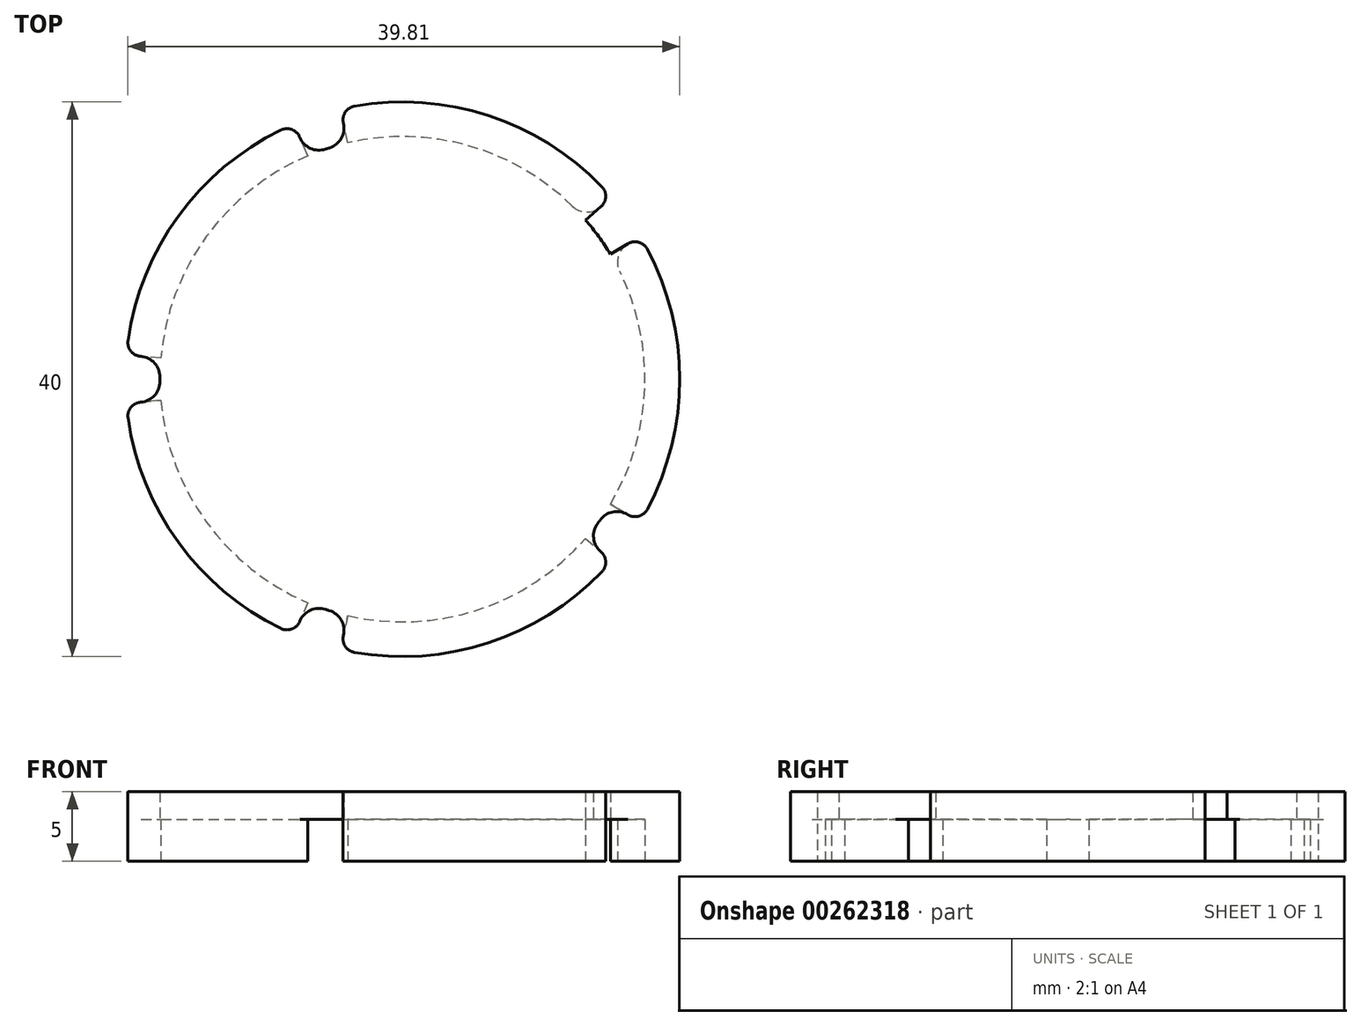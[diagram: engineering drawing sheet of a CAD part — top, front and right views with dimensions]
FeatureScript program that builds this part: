
annotation { "Feature Type Name" : "Feature", "Feature Type Description" : "" }
export const myFeature = defineFeature(function(context is Context, id is Id, definition is map)
    precondition{}
    {
        {
            var Q0;
            Q0=qCreatedBy(makeId("Top.planeOp"),FACE);
            var sketch = newSketch(context, id + "F0", { "sketchPlane" : qUnion([Q0])});
            skCircle(sketch, "E0", {"center": v(0, 0) * mm, "radius": 17.5 * mm});
            skArc(sketch, "E1", {"start": v(-7.81, 18.41) * mm, "mid": v(-16.18, 11.76) * mm, "end": v(-19.92, 1.74) * mm});
            skLineSegment(sketch, "E2", {"start": v(0, 0) * mm, "end": v(-17.43, 1.53) * mm, "construction": true});
            skLineSegment(sketch, "E3", {"start": v(-17.43, 1.53) * mm, "end": v(-19.92, 1.74) * mm});
            skLineSegment(sketch, "E4.MirrorCS", {"start": v(-17.43, -1.53) * mm, "end": v(-19.92, -1.74) * mm});
            skLineSegment(sketch, "E5.1.0", {"start": v(-6.84, -16.1) * mm, "end": v(-7.81, -18.41) * mm});
            skLineSegment(sketch, "E5.1.1", {"start": v(-3.94, -17.05) * mm, "end": v(-4.5, -19.49) * mm});
            skLineSegment(sketch, "E5.2.0", {"start": v(13.2, -11.48) * mm, "end": v(15.1, -13.12) * mm});
            skLineSegment(sketch, "E5.2.1", {"start": v(15, -9.01) * mm, "end": v(17.14, -10.3) * mm});
            skLineSegment(sketch, "E5.3.0", {"start": v(15, 9.01) * mm, "end": v(17.14, 10.3) * mm});
            skLineSegment(sketch, "E5.3.1", {"start": v(13.2, 11.48) * mm, "end": v(15.1, 13.12) * mm});
            skLineSegment(sketch, "E5.4.0", {"start": v(-3.94, 17.05) * mm, "end": v(-4.5, 19.49) * mm});
            skLineSegment(sketch, "E5.4.1", {"start": v(-6.84, 16.1) * mm, "end": v(-7.81, 18.41) * mm});
            skArc(sketch, "E6.trimOffspring", {"start": v(15.1, 13.12) * mm, "mid": v(6.18, 19.02) * mm, "end": v(-4.5, 19.49) * mm});
            skArc(sketch, "E7.trimOffspring", {"start": v(17.14, -10.3) * mm, "mid": v(20, 0) * mm, "end": v(17.14, 10.3) * mm});
            skArc(sketch, "E8.trimOffspring", {"start": v(-4.5, -19.49) * mm, "mid": v(6.18, -19.02) * mm, "end": v(15.1, -13.12) * mm});
            skArc(sketch, "E9.trimOffspring", {"start": v(-19.92, -1.74) * mm, "mid": v(-16.18, -11.76) * mm, "end": v(-7.81, -18.41) * mm});
            skSolve(sketch);
        }
        {
            var Q0;
            {var subQ0=sQuery(id+"F0.wireOp",EDGE,"E0");var subQ5=makeQuery(id+"F0.imprint","INTERSECT",VERTEX,{"derivedFrom":[subQ0,sQuery(id+"F0.wireOp",EDGE,"E5.3.0")]});Q0=makeQuery(id+"F0.imprint","IMPRINT",FACE,{"disambiguationData":[TD([[makeQuery(id+"F0.imprint","IMPRINT",EDGE,{"disambiguationData":[TD([[subQ5,-1.0]])],"derivedFrom":subQ0}),1.0]])]});}
            extrude(context, id + "F1", {"entities" : qUnion([Q0]), "depth" : 2 * mm});
        }
        {
            var Q0;
            {var subQ0=sQuery(id+"F0.wireOp",EDGE,"E5.2.1");Q0=makeQuery(id+"F0.imprint","IMPRINT",FACE,{"disambiguationData":[TD([[makeQuery(id+"F0.imprint","IMPRINT",EDGE,{"derivedFrom":subQ0}),1.0]])]});}
            var Q1;
            {var subQ0=sQuery(id+"F0.wireOp",EDGE,"E5.3.1");Q1=makeQuery(id+"F0.imprint","IMPRINT",FACE,{"disambiguationData":[TD([[makeQuery(id+"F0.imprint","IMPRINT",EDGE,{"derivedFrom":subQ0}),1.0]])]});}
            var Q2;
            Q2=makeQuery(id+"F0.imprint","IMPRINT",FACE,{"disambiguationData":[TD([[makeQuery(id+"F0.imprint","IMPRINT",EDGE,{"derivedFrom":sQuery(id+"F0.wireOp",EDGE,"E1")}),1.0]])]});
            var Q3;
            {var subQ0=sQuery(id+"F0.wireOp",EDGE,"E4.MirrorCS");Q3=makeQuery(id+"F0.imprint","IMPRINT",FACE,{"disambiguationData":[TD([[makeQuery(id+"F0.imprint","IMPRINT",EDGE,{"derivedFrom":subQ0}),1.0]])]});}
            var Q4;
            {var subQ0=sQuery(id+"F0.wireOp",EDGE,"E5.1.1");Q4=makeQuery(id+"F0.imprint","IMPRINT",FACE,{"disambiguationData":[TD([[makeQuery(id+"F0.imprint","IMPRINT",EDGE,{"derivedFrom":subQ0}),1.0]])]});}
            extrude(context, id + "F2", {"entities" : qUnion([Q0, Q1, Q2, Q3, Q4]), "operationType" : NewBodyOperationType.ADD, "depth" : 2 * mm, "hasSecondDirection" : true, "secondDirectionOppositeDirection" : true, "secondDirectionDepth" : 3 * mm});
        }
        {
            var Q0;
            {var subQ0=sQuery(id+"F0.wireOp",EDGE,"E0");var subQ1=sQuery(id+"F0.wireOp",EDGE,"E5.1.0");Q0=makeQuery(id+"F2.boolean.opBoolean","SPLIT",EDGE,{"disambiguationData":[topologyDisambiguationEdgeConnected([makeQuery(id+"F1.opExtrude","SWEPT_FACE",FACE,{"disambiguationData":[OSD([subQ0])]})])],"derivedFrom":makeQuery(id+"F2.opExtrude","SWEPT_EDGE",EDGE,{"disambiguationData":[OSD([subQ0,subQ1])]})});}
            var Q1;
            {var subQ0=sQuery(id+"F0.wireOp",EDGE,"E0");var subQ1=sQuery(id+"F0.wireOp",EDGE,"E5.1.1");Q1=makeQuery(id+"F2.boolean.opBoolean","SPLIT",EDGE,{"disambiguationData":[topologyDisambiguationEdgeConnected([makeQuery(id+"F1.opExtrude","SWEPT_FACE",FACE,{"disambiguationData":[OSD([subQ0])]})])],"derivedFrom":makeQuery(id+"F2.opExtrude","SWEPT_EDGE",EDGE,{"disambiguationData":[OSD([subQ0,subQ1])]})});}
            var Q2;
            {var subQ0=sQuery(id+"F0.wireOp",EDGE,"E0");var subQ1=sQuery(id+"F0.wireOp",EDGE,"E3");Q2=makeQuery(id+"F2.boolean.opBoolean","SPLIT",EDGE,{"disambiguationData":[topologyDisambiguationEdgeConnected([makeQuery(id+"F1.opExtrude","SWEPT_FACE",FACE,{"disambiguationData":[OSD([subQ0])]})])],"derivedFrom":makeQuery(id+"F2.opExtrude","SWEPT_EDGE",EDGE,{"disambiguationData":[OSD([subQ0,subQ1])]})});}
            var Q3;
            {var subQ0=sQuery(id+"F0.wireOp",EDGE,"E0");var subQ1=sQuery(id+"F0.wireOp",EDGE,"E4.MirrorCS");Q3=makeQuery(id+"F2.boolean.opBoolean","SPLIT",EDGE,{"disambiguationData":[topologyDisambiguationEdgeConnected([makeQuery(id+"F1.opExtrude","SWEPT_FACE",FACE,{"disambiguationData":[OSD([subQ0])]})])],"derivedFrom":makeQuery(id+"F2.opExtrude","SWEPT_EDGE",EDGE,{"disambiguationData":[OSD([subQ0,subQ1])]})});}
            var Q4;
            {var subQ0=sQuery(id+"F0.wireOp",EDGE,"E0");var subQ1=sQuery(id+"F0.wireOp",EDGE,"E5.4.0");Q4=makeQuery(id+"F2.boolean.opBoolean","SPLIT",EDGE,{"disambiguationData":[topologyDisambiguationEdgeConnected([makeQuery(id+"F1.opExtrude","SWEPT_FACE",FACE,{"disambiguationData":[OSD([subQ0])]})])],"derivedFrom":makeQuery(id+"F2.opExtrude","SWEPT_EDGE",EDGE,{"disambiguationData":[OSD([subQ0,subQ1])]})});}
            var Q5;
            {var subQ0=sQuery(id+"F0.wireOp",EDGE,"E0");var subQ1=sQuery(id+"F0.wireOp",EDGE,"E5.4.1");Q5=makeQuery(id+"F2.boolean.opBoolean","SPLIT",EDGE,{"disambiguationData":[topologyDisambiguationEdgeConnected([makeQuery(id+"F1.opExtrude","SWEPT_FACE",FACE,{"disambiguationData":[OSD([subQ0])]})])],"derivedFrom":makeQuery(id+"F2.opExtrude","SWEPT_EDGE",EDGE,{"disambiguationData":[OSD([subQ0,subQ1])]})});}
            var Q6;
            {var subQ0=sQuery(id+"F0.wireOp",EDGE,"E0");var subQ1=sQuery(id+"F0.wireOp",EDGE,"E5.3.0");Q6=makeQuery(id+"F2.boolean.opBoolean","SPLIT",EDGE,{"disambiguationData":[topologyDisambiguationEdgeConnected([makeQuery(id+"F1.opExtrude","SWEPT_FACE",FACE,{"disambiguationData":[OSD([subQ0])]})])],"derivedFrom":makeQuery(id+"F2.opExtrude","SWEPT_EDGE",EDGE,{"disambiguationData":[OSD([subQ0,subQ1])]})});}
            var Q7;
            {var subQ0=sQuery(id+"F0.wireOp",EDGE,"E0");var subQ1=sQuery(id+"F0.wireOp",EDGE,"E5.3.1");Q7=makeQuery(id+"F2.boolean.opBoolean","SPLIT",EDGE,{"disambiguationData":[topologyDisambiguationEdgeConnected([makeQuery(id+"F1.opExtrude","SWEPT_FACE",FACE,{"disambiguationData":[OSD([subQ0])]})])],"derivedFrom":makeQuery(id+"F2.opExtrude","SWEPT_EDGE",EDGE,{"disambiguationData":[OSD([subQ0,subQ1])]})});}
            var Q8;
            {var subQ0=sQuery(id+"F0.wireOp",EDGE,"E0");var subQ1=sQuery(id+"F0.wireOp",EDGE,"E5.2.1");Q8=makeQuery(id+"F2.boolean.opBoolean","SPLIT",EDGE,{"disambiguationData":[topologyDisambiguationEdgeConnected([makeQuery(id+"F1.opExtrude","SWEPT_FACE",FACE,{"disambiguationData":[OSD([subQ0])]})])],"derivedFrom":makeQuery(id+"F2.opExtrude","SWEPT_EDGE",EDGE,{"disambiguationData":[OSD([subQ0,subQ1])]})});}
            var Q9;
            {var subQ0=sQuery(id+"F0.wireOp",EDGE,"E0");var subQ1=sQuery(id+"F0.wireOp",EDGE,"E5.2.0");Q9=makeQuery(id+"F2.boolean.opBoolean","SPLIT",EDGE,{"disambiguationData":[topologyDisambiguationEdgeConnected([makeQuery(id+"F1.opExtrude","SWEPT_FACE",FACE,{"disambiguationData":[OSD([subQ0])]})])],"derivedFrom":makeQuery(id+"F2.opExtrude","SWEPT_EDGE",EDGE,{"disambiguationData":[OSD([subQ0,subQ1])]})});}
            fillet(context, id + "F3", {"entities" : qUnion([Q0, Q1, Q2, Q3, Q4, Q5, Q6, Q7, Q8, Q9]), "radius" : 1.5 * mm, "tangentPropagation" : true, "allowEdgeOverflow" : false});
        }
        {
            var Q0;
            Q0=makeQuery(id+"F2.opExtrude","SWEPT_EDGE",EDGE,{"disambiguationData":[OSD([sQuery(id+"F0.wireOp",EDGE,"E5.2.0"),sQuery(id+"F0.wireOp",EDGE,"E8.trimOffspring")])]});
            var Q1;
            Q1=makeQuery(id+"F2.opExtrude","SWEPT_EDGE",EDGE,{"disambiguationData":[OSD([sQuery(id+"F0.wireOp",EDGE,"E5.2.1"),sQuery(id+"F0.wireOp",EDGE,"E7.trimOffspring")])]});
            var Q2;
            Q2=makeQuery(id+"F2.opExtrude","SWEPT_EDGE",EDGE,{"disambiguationData":[OSD([sQuery(id+"F0.wireOp",EDGE,"E5.3.0"),sQuery(id+"F0.wireOp",EDGE,"E7.trimOffspring")])]});
            var Q3;
            Q3=makeQuery(id+"F2.opExtrude","SWEPT_EDGE",EDGE,{"disambiguationData":[OSD([sQuery(id+"F0.wireOp",EDGE,"E5.3.1"),sQuery(id+"F0.wireOp",EDGE,"E6.trimOffspring")])]});
            var Q4;
            Q4=makeQuery(id+"F2.opExtrude","SWEPT_EDGE",EDGE,{"disambiguationData":[OSD([sQuery(id+"F0.wireOp",EDGE,"E5.4.0"),sQuery(id+"F0.wireOp",EDGE,"E6.trimOffspring")])]});
            var Q5;
            Q5=makeQuery(id+"F2.opExtrude","SWEPT_EDGE",EDGE,{"disambiguationData":[OSD([sQuery(id+"F0.wireOp",EDGE,"E1"),sQuery(id+"F0.wireOp",EDGE,"E5.4.1")])]});
            var Q6;
            Q6=makeQuery(id+"F2.opExtrude","SWEPT_EDGE",EDGE,{"disambiguationData":[OSD([sQuery(id+"F0.wireOp",EDGE,"E1"),sQuery(id+"F0.wireOp",EDGE,"E3")])]});
            var Q7;
            Q7=makeQuery(id+"F2.opExtrude","SWEPT_EDGE",EDGE,{"disambiguationData":[OSD([sQuery(id+"F0.wireOp",EDGE,"E4.MirrorCS"),sQuery(id+"F0.wireOp",EDGE,"E9.trimOffspring")])]});
            var Q8;
            Q8=makeQuery(id+"F2.opExtrude","SWEPT_EDGE",EDGE,{"disambiguationData":[OSD([sQuery(id+"F0.wireOp",EDGE,"E5.1.1"),sQuery(id+"F0.wireOp",EDGE,"E8.trimOffspring")])]});
            var Q9;
            Q9=makeQuery(id+"F2.opExtrude","SWEPT_EDGE",EDGE,{"disambiguationData":[OSD([sQuery(id+"F0.wireOp",EDGE,"E5.1.0"),sQuery(id+"F0.wireOp",EDGE,"E9.trimOffspring")])]});
            fillet(context, id + "F4", {"entities" : qUnion([Q0, Q1, Q2, Q3, Q4, Q5, Q6, Q7, Q8, Q9]), "radius" : 1 * mm, "tangentPropagation" : true, "allowEdgeOverflow" : false});
        }
    });
